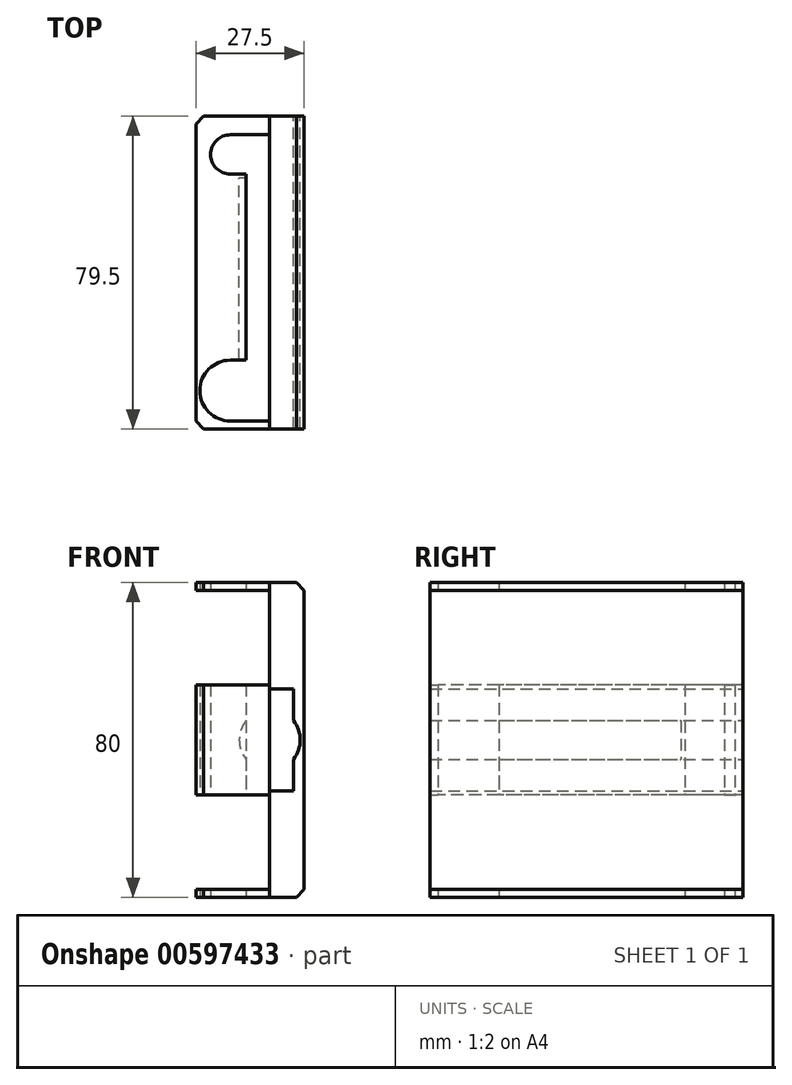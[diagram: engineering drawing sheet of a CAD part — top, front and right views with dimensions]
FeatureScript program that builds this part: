
annotation { "Feature Type Name" : "Feature", "Feature Type Description" : "" }
export const myFeature = defineFeature(function(context is Context, id is Id, definition is map)
    precondition{}
    {
        {
            var Q0;
            Q0=qCreatedBy(makeId("Right.planeOp"),FACE);
            var sketch = newSketch(context, id + "F0", { "sketchPlane" : qUnion([Q0])});
            skLineSegment(sketch, "E0", {"start": v(-7, -26) * mm, "end": v(-7, 26) * mm, "construction": true});
            skLineSegment(sketch, "E1", {"start": v(-38, -11) * mm, "end": v(38, -11) * mm, "construction": true});
            skPoint(sketch, "E2", {"position": v(-7, 0) * mm});
            skPoint(sketch, "E3", {"position": v(0, -11) * mm});
            skLineSegment(sketch, "E4.MirrorCS", {"start": v(7, -26) * mm, "end": v(7, 26) * mm, "construction": true});
            skLineSegment(sketch, "E5.MirrorCS", {"start": v(-38, 11) * mm, "end": v(38, 11) * mm, "construction": true});
            skArc(sketch, "E6", {"start": v(-17, -11) * mm, "mid": v(-9.93, -13.93) * mm, "end": v(-7, -21) * mm, "construction": true});
            skArc(sketch, "E7.MirrorCS", {"start": v(17, -11) * mm, "mid": v(9.93, -13.93) * mm, "end": v(7, -21) * mm, "construction": true});
            skArc(sketch, "E8.MirrorCS", {"start": v(-17, 11) * mm, "mid": v(-9.93, 13.93) * mm, "end": v(-7, 21) * mm, "construction": true});
            skArc(sketch, "E9.MirrorCS", {"start": v(17, 11) * mm, "mid": v(9.93, 13.93) * mm, "end": v(7, 21) * mm, "construction": true});
            skLineSegment(sketch, "E10", {"start": v(-30, 26) * mm, "end": v(-30, -26) * mm, "construction": true});
            skLineSegment(sketch, "E11.MirrorCS", {"start": v(30, 26) * mm, "end": v(30, -26) * mm, "construction": true});
            skSolve(sketch);
        }
        {
            var Q0;
            Q0=qCreatedBy(makeId("Top.planeOp"),FACE);
            var sketch = newSketch(context, id + "F1", { "sketchPlane" : qUnion([Q0])});
            skArc(sketch, "E12", {"start": v(-10, 37.75) * mm, "mid": v(-17.75, 30) * mm, "end": v(-10, 22.25) * mm});
            skLineSegment(sketch, "E13", {"start": v(-10, 39.75) * mm, "end": v(0, 39.75) * mm});
            skLineSegment(sketch, "E14", {"start": v(-10, 39.75) * mm, "end": v(-16.75, 39.75) * mm});
            skLineSegment(sketch, "E15", {"start": v(-16.75, 39.75) * mm, "end": v(-18.75, 37.75) * mm});
            skArc(sketch, "E16.MirrorCS", {"start": v(-10, -37.75) * mm, "mid": v(-17.75, -30) * mm, "end": v(-10, -22.25) * mm});
            skLineSegment(sketch, "E17.MirrorCS", {"start": v(-10, -39.75) * mm, "end": v(-16.75, -39.75) * mm});
            skLineSegment(sketch, "E18.MirrorCS", {"start": v(-10, -39.75) * mm, "end": v(0, -39.75) * mm});
            skLineSegment(sketch, "E19.MirrorCS", {"start": v(-16.75, -39.75) * mm, "end": v(-18.75, -37.75) * mm});
            skLineSegment(sketch, "E20", {"start": v(-18.75, 37.75) * mm, "end": v(-18.75, -37.75) * mm});
            skLineSegment(sketch, "E21", {"start": v(-6, 22.25) * mm, "end": v(-6, -22.25) * mm});
            skLineSegment(sketch, "E22", {"start": v(-6, -22.25) * mm, "end": v(-10, -22.25) * mm});
            skLineSegment(sketch, "E23", {"start": v(-6, 22.25) * mm, "end": v(-10, 22.25) * mm});
            skArc(sketch, "E24", {"start": v(-10, 35) * mm, "mid": v(-15, 30) * mm, "end": v(-10, 25) * mm});
            skLineSegment(sketch, "E25", {"start": v(-10, 35) * mm, "end": v(0, 35) * mm});
            skLineSegment(sketch, "E26", {"start": v(0, 35) * mm, "end": v(0, 39.75) * mm});
            skLineSegment(sketch, "E27", {"start": v(-10, 25) * mm, "end": v(-6, 25) * mm});
            skLineSegment(sketch, "E28", {"start": v(-6, 25) * mm, "end": v(-6, 22.25) * mm});
            skArc(sketch, "E29.MirrorCS", {"start": v(-10, -35) * mm, "mid": v(-15, -30) * mm, "end": v(-10, -25) * mm});
            skLineSegment(sketch, "E30.MirrorCS", {"start": v(-10, -35) * mm, "end": v(0, -35) * mm});
            skLineSegment(sketch, "E31.MirrorCS", {"start": v(0, -35) * mm, "end": v(0, -39.75) * mm});
            skLineSegment(sketch, "E32.MirrorCS", {"start": v(-10, -25) * mm, "end": v(-6, -25) * mm});
            skLineSegment(sketch, "E33.MirrorCS", {"start": v(-6, -25) * mm, "end": v(-6, -22.25) * mm});
            skLineSegment(sketch, "E34", {"start": v(-10, 37.75) * mm, "end": v(0, 37.75) * mm});
            skLineSegment(sketch, "E35", {"start": v(-10, -37.75) * mm, "end": v(0, -37.75) * mm});
            skSolve(sketch);
        }
        {
            var Q0;
            Q0=makeQuery(id+"F1.imprint","IMPRINT",FACE,{"disambiguationData":[TD([[makeQuery(id+"F1.imprint","IMPRINT",EDGE,{"derivedFrom":sQuery(id+"F1.wireOp",EDGE,"E12")}),-1.0]])]});
            var Q1;
            Q1=makeQuery(id+"F1.imprint","IMPRINT",FACE,{"disambiguationData":[TD([[makeQuery(id+"F1.imprint","IMPRINT",EDGE,{"derivedFrom":sQuery(id+"F1.wireOp",EDGE,"E12")}),1.0]])]});
            var Q2;
            Q2=makeQuery(id+"F1.imprint","IMPRINT",FACE,{"disambiguationData":[TD([[makeQuery(id+"F1.imprint","IMPRINT",EDGE,{"derivedFrom":sQuery(id+"F1.wireOp",EDGE,"E16.MirrorCS")}),-1.0]])]});
            extrude(context, id + "F2", {"entities" : qUnion([Q0, Q1, Q2]), "endBound" : BoundingType.SYMMETRIC, "depth" : 80 * mm, "offsetDistance" : 25 * mm});
        }
        {
            var Q0;
            Q0=makeQuery(id+"F1.imprint","IMPRINT",FACE,{"disambiguationData":[TD([[makeQuery(id+"F1.imprint","IMPRINT",EDGE,{"derivedFrom":sQuery(id+"F1.wireOp",EDGE,"E12")}),1.0]])]});
            var Q1;
            Q1=makeQuery(id+"F1.imprint","IMPRINT",FACE,{"disambiguationData":[TD([[makeQuery(id+"F1.imprint","IMPRINT",EDGE,{"derivedFrom":sQuery(id+"F1.wireOp",EDGE,"E16.MirrorCS")}),-1.0]])]});
            extrude(context, id + "F3", {"entities" : qUnion([Q0, Q1]), "operationType" : NewBodyOperationType.REMOVE, "depth" : 38 * mm, "offsetDistance" : 25 * mm, "hasSecondDirection" : true, "secondDirectionOppositeDirection" : false, "secondDirectionDepth" : 14 * mm});
        }
        {
            var Q0;
            Q0=makeQuery(id+"F1.imprint","IMPRINT",FACE,{"disambiguationData":[TD([[makeQuery(id+"F1.imprint","IMPRINT",EDGE,{"derivedFrom":sQuery(id+"F1.wireOp",EDGE,"E16.MirrorCS")}),-1.0]])]});
            var Q1;
            Q1=makeQuery(id+"F1.imprint","IMPRINT",FACE,{"disambiguationData":[TD([[makeQuery(id+"F1.imprint","IMPRINT",EDGE,{"derivedFrom":sQuery(id+"F1.wireOp",EDGE,"E12")}),1.0]])]});
            extrude(context, id + "F4", {"entities" : qUnion([Q0, Q1]), "operationType" : NewBodyOperationType.REMOVE, "oppositeDirection" : true, "depth" : 38 * mm, "offsetDistance" : 25 * mm, "hasSecondDirection" : true, "secondDirectionOppositeDirection" : true, "secondDirectionDepth" : 14 * mm});
        }
        {
            var Q0;
            Q0=qCreatedBy(makeId("Front.planeOp"),FACE);
            var sketch = newSketch(context, id + "F5", { "sketchPlane" : qUnion([Q0])});
            skCircle(sketch, "E36", {"center": v(0, 0) * mm, "radius": 7.75 * mm});
            skLineSegment(sketch, "E37", {"start": v(0, 40) * mm, "end": v(6.75, 40) * mm});
            skLineSegment(sketch, "E38", {"start": v(6.75, 40) * mm, "end": v(8.75, 38) * mm});
            skLineSegment(sketch, "E39.MirrorCS", {"start": v(6.75, -40) * mm, "end": v(8.75, -38) * mm});
            skLineSegment(sketch, "E40.MirrorCS", {"start": v(0, -40) * mm, "end": v(6.75, -40) * mm});
            skLineSegment(sketch, "E41", {"start": v(8.75, 38) * mm, "end": v(8.75, -38) * mm});
            skLineSegment(sketch, "E42", {"start": v(0, 40) * mm, "end": v(0, 13) * mm});
            skPoint(sketch, "E43", {"position": v(0, 14) * mm});
            skLineSegment(sketch, "E44", {"start": v(0, 13) * mm, "end": v(6, 13) * mm});
            skLineSegment(sketch, "E45", {"start": v(6, 13) * mm, "end": v(6, 4.9) * mm});
            skLineSegment(sketch, "E46.MirrorCS", {"start": v(0, -40) * mm, "end": v(0, -13) * mm});
            skLineSegment(sketch, "E47.MirrorCS", {"start": v(0, -13) * mm, "end": v(6, -13) * mm});
            skLineSegment(sketch, "E48.MirrorCS", {"start": v(6, -13) * mm, "end": v(6, -4.9) * mm});
            skSolve(sketch);
        }
        {
            var Q0;
            Q0=makeQuery(id+"F5.imprint","IMPRINT",FACE,{"disambiguationData":[TD([[makeQuery(id+"F5.imprint","IMPRINT",EDGE,{"derivedFrom":sQuery(id+"F5.wireOp",EDGE,"E36")}),1.0]])]});
            extrude(context, id + "F6", {"entities" : qUnion([Q0]), "operationType" : NewBodyOperationType.REMOVE, "endBound" : BoundingType.SYMMETRIC, "depth" : 48 * mm, "offsetDistance" : 25 * mm});
        }
        {
            var Q0;
            Q0=makeQuery(id+"F5.imprint","IMPRINT",FACE,{"disambiguationData":[TD([[makeQuery(id+"F5.imprint","IMPRINT",EDGE,{"derivedFrom":sQuery(id+"F5.wireOp",EDGE,"E37")}),-1.0]])]});
            extrude(context, id + "F7", {"entities" : qUnion([Q0]), "endBound" : BoundingType.SYMMETRIC, "depth" : 79.5 * mm, "offsetDistance" : 25 * mm});
        }
    });
